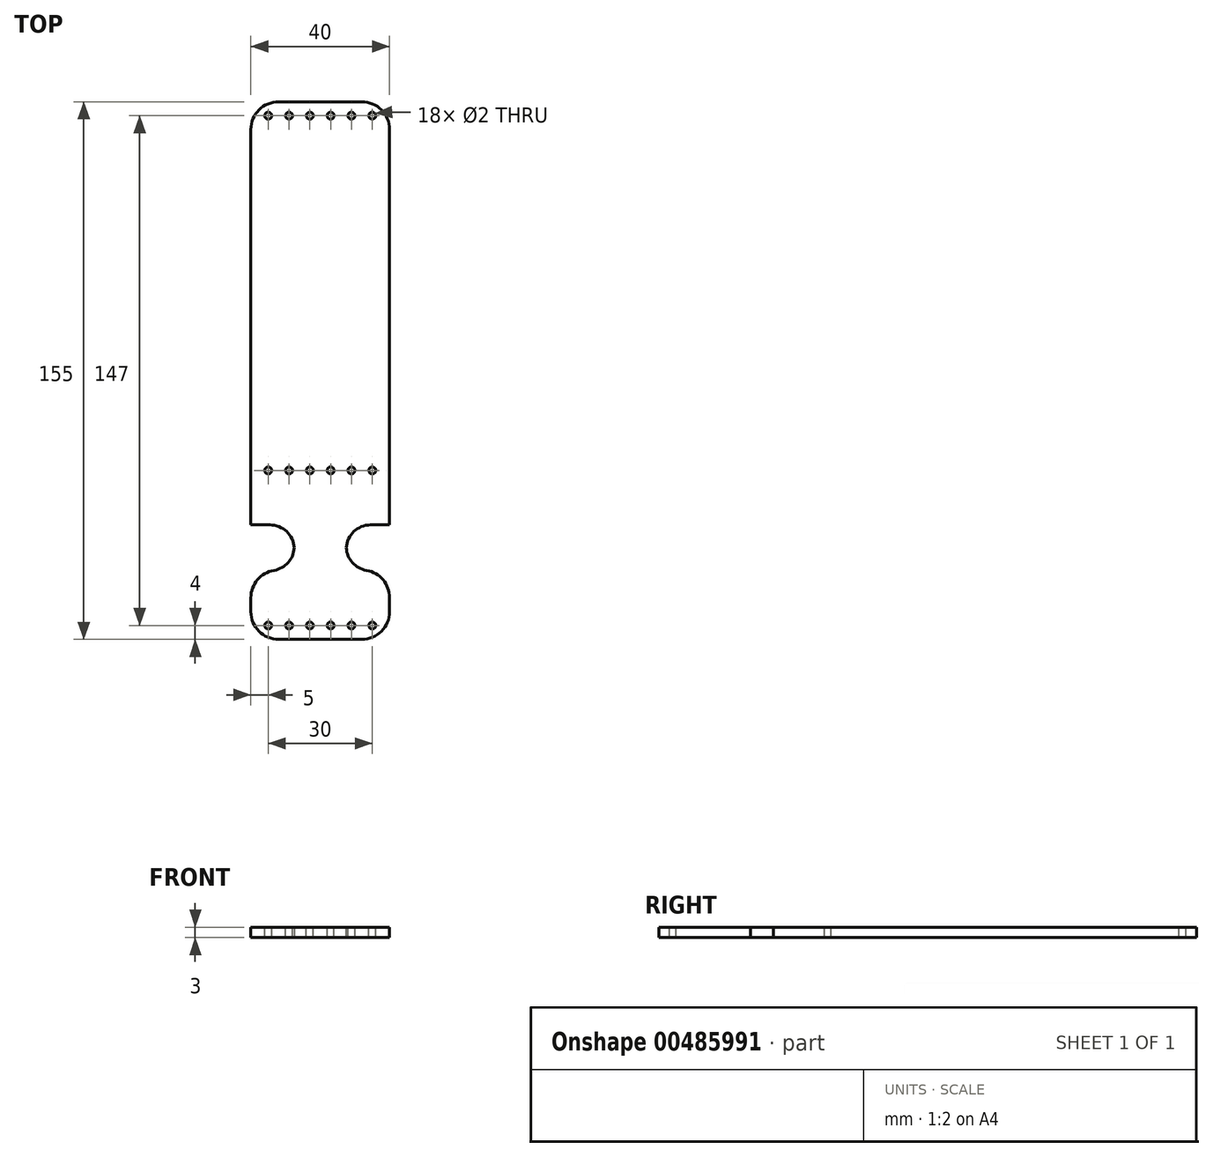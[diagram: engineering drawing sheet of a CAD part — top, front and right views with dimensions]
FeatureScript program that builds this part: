
annotation { "Feature Type Name" : "Feature", "Feature Type Description" : "" }
export const myFeature = defineFeature(function(context is Context, id is Id, definition is map)
    precondition{}
    {
        {
            var Q0;
            Q0=qCreatedBy(makeId("Top.planeOp"),FACE);
            var sketch = newSketch(context, id + "F0", { "sketchPlane" : qUnion([Q0])});
            skLineSegment(sketch, "E0.bottom", {"start": v(-20, 77.5) * mm, "end": v(20, 77.5) * mm});
            skLineSegment(sketch, "E0.top", {"start": v(-20, -77.5) * mm, "end": v(20, -77.5) * mm});
            skLineSegment(sketch, "E0.left", {"start": v(-20, 77.5) * mm, "end": v(-20, -77.5) * mm});
            skLineSegment(sketch, "E0.right", {"start": v(20, 77.5) * mm, "end": v(20, -77.5) * mm});
            skSolve(sketch);
        }
        {
            var Q0;
            Q0=qSketchRegion(id+"F0",true);
            extrude(context, id + "F1", {"entities" : qUnion([Q0]), "depth" : 3 * mm});
        }
        {
            var Q0;
            Q0=makeQuery(id+"F1.opExtrude","CAP_FACE",FACE,{"disambiguationData":[OSD([sQuery(id+"F0.wireOp",EDGE,"E0.bottom"),sQuery(id+"F0.wireOp",EDGE,"E0.top"),sQuery(id+"F0.wireOp",EDGE,"E0.left"),sQuery(id+"F0.wireOp",EDGE,"E0.right")])],"isStart":false});
            var sketch = newSketch(context, id + "F2", { "sketchPlane" : qUnion([Q0])});
            skLineSegment(sketch, "E1.bottom", {"start": v(-20, -57.5) * mm, "end": v(20, -57.5) * mm});
            skLineSegment(sketch, "E1.top", {"start": v(-20, -44.5) * mm, "end": v(20, -44.5) * mm});
            skLineSegment(sketch, "E1.left", {"start": v(-20, -57.5) * mm, "end": v(-20, -44.5) * mm});
            skLineSegment(sketch, "E1.right", {"start": v(20, -57.5) * mm, "end": v(20, -44.5) * mm});
            skLineSegment(sketch, "E2.bottom", {"start": v(-7.5, -44.5) * mm, "end": v(7.5, -44.5) * mm});
            skLineSegment(sketch, "E2.top", {"start": v(-7.5, -57.5) * mm, "end": v(7.5, -57.5) * mm});
            skLineSegment(sketch, "E2.left", {"start": v(-7.5, -44.5) * mm, "end": v(-7.5, -57.5) * mm});
            skLineSegment(sketch, "E2.right", {"start": v(7.5, -44.5) * mm, "end": v(7.5, -57.5) * mm});
            skSolve(sketch);
        }
        {
            var Q0;
            {var subQ0=sQuery(id+"F2.wireOp",EDGE,"E1.left");Q0=makeQuery(id+"F2.imprint","IMPRINT",FACE,{"disambiguationData":[TD([[makeQuery(id+"F2.imprint","IMPRINT",EDGE,{"derivedFrom":subQ0}),1.0]])]});}
            var Q1;
            {var subQ0=sQuery(id+"F2.wireOp",EDGE,"E1.right");Q1=makeQuery(id+"F2.imprint","IMPRINT",FACE,{"disambiguationData":[TD([[makeQuery(id+"F2.imprint","IMPRINT",EDGE,{"derivedFrom":subQ0}),-1.0]])]});}
            extrude(context, id + "F3", {"entities" : qUnion([Q0, Q1]), "operationType" : NewBodyOperationType.REMOVE, "endBound" : BoundingType.UP_TO_NEXT, "oppositeDirection" : true, "depth" : 25 * mm});
        }
        {
            var Q0;
            Q0=makeQuery(id+"F3.boolean.opBoolean","COPY",EDGE,{"derivedFrom":makeQuery(id+"F3.opExtrude","SWEPT_EDGE",EDGE,{"disambiguationData":[OSD([sQuery(id+"F0.wireOp",EDGE,"E0.left"),sQuery(id+"F2.wireOp",EDGE,"E1.top"),sQuery(id+"F2.wireOp",EDGE,"E1.left")])]})});
            var Q1;
            Q1=makeQuery(id+"F3.boolean.opBoolean","COPY",EDGE,{"derivedFrom":makeQuery(id+"F3.opExtrude","SWEPT_EDGE",EDGE,{"disambiguationData":[OSD([sQuery(id+"F0.wireOp",EDGE,"E0.right"),sQuery(id+"F2.wireOp",EDGE,"E1.top"),sQuery(id+"F2.wireOp",EDGE,"E1.right")])]})});
            var Q2;
            Q2=makeQuery(id+"F3.boolean.opBoolean","COPY",EDGE,{"derivedFrom":makeQuery(id+"F3.opExtrude","SWEPT_EDGE",EDGE,{"disambiguationData":[OSD([sQuery(id+"F0.wireOp",EDGE,"E0.right"),sQuery(id+"F2.wireOp",EDGE,"E1.bottom"),sQuery(id+"F2.wireOp",EDGE,"E1.right")])]})});
            var Q3;
            Q3=makeQuery(id+"F3.boolean.opBoolean","COPY",EDGE,{"derivedFrom":makeQuery(id+"F3.opExtrude","SWEPT_EDGE",EDGE,{"disambiguationData":[OSD([sQuery(id+"F0.wireOp",EDGE,"E0.left"),sQuery(id+"F2.wireOp",EDGE,"E1.bottom"),sQuery(id+"F2.wireOp",EDGE,"E1.left")])]})});
            var Q4;
            Q4=makeQuery(id+"F1.opExtrude","SWEPT_EDGE",EDGE,{"disambiguationData":[OSD([sQuery(id+"F0.wireOp",EDGE,"E0.top"),sQuery(id+"F0.wireOp",EDGE,"E0.left")])]});
            var Q5;
            Q5=makeQuery(id+"F1.opExtrude","SWEPT_EDGE",EDGE,{"disambiguationData":[OSD([sQuery(id+"F0.wireOp",EDGE,"E0.top"),sQuery(id+"F0.wireOp",EDGE,"E0.right")])]});
            var Q6;
            Q6=makeQuery(id+"F1.opExtrude","SWEPT_EDGE",EDGE,{"disambiguationData":[OSD([sQuery(id+"F0.wireOp",EDGE,"E0.bottom"),sQuery(id+"F0.wireOp",EDGE,"E0.left")])]});
            var Q7;
            Q7=makeQuery(id+"F1.opExtrude","SWEPT_EDGE",EDGE,{"disambiguationData":[OSD([sQuery(id+"F0.wireOp",EDGE,"E0.bottom"),sQuery(id+"F0.wireOp",EDGE,"E0.right")])]});
            fillet(context, id + "F4", {"entities" : qUnion([Q0, Q1, Q2, Q3, Q4, Q5, Q6, Q7]), "radius" : 8 * mm, "tangentPropagation" : true, "allowEdgeOverflow" : false});
        }
        {
            var Q0;
            Q0=makeQuery(id+"F3.boolean.opBoolean","COPY",EDGE,{"derivedFrom":makeQuery(id+"F3.opExtrude","SWEPT_EDGE",EDGE,{"disambiguationData":[OSD([sQuery(id+"F2.wireOp",EDGE,"E1.top"),sQuery(id+"F2.wireOp",EDGE,"E2.bottom"),sQuery(id+"F2.wireOp",EDGE,"E2.left")])]})});
            var Q1;
            Q1=makeQuery(id+"F3.boolean.opBoolean","COPY",EDGE,{"derivedFrom":makeQuery(id+"F3.opExtrude","SWEPT_EDGE",EDGE,{"disambiguationData":[OSD([sQuery(id+"F2.wireOp",EDGE,"E1.bottom"),sQuery(id+"F2.wireOp",EDGE,"E2.top"),sQuery(id+"F2.wireOp",EDGE,"E2.left")])]})});
            var Q2;
            Q2=makeQuery(id+"F3.boolean.opBoolean","COPY",EDGE,{"derivedFrom":makeQuery(id+"F3.opExtrude","SWEPT_EDGE",EDGE,{"disambiguationData":[OSD([sQuery(id+"F2.wireOp",EDGE,"E1.top"),sQuery(id+"F2.wireOp",EDGE,"E2.bottom"),sQuery(id+"F2.wireOp",EDGE,"E2.right")])]})});
            var Q3;
            Q3=makeQuery(id+"F3.boolean.opBoolean","COPY",EDGE,{"derivedFrom":makeQuery(id+"F3.opExtrude","SWEPT_EDGE",EDGE,{"disambiguationData":[OSD([sQuery(id+"F2.wireOp",EDGE,"E1.bottom"),sQuery(id+"F2.wireOp",EDGE,"E2.top"),sQuery(id+"F2.wireOp",EDGE,"E2.right")])]})});
            fillet(context, id + "F5", {"entities" : qUnion([Q0, Q1, Q2, Q3]), "radius" : 7 * mm, "tangentPropagation" : true, "allowEdgeOverflow" : false});
        }
        {
            var Q0;
            Q0=makeQuery(id+"F1.opExtrude","CAP_FACE",FACE,{"disambiguationData":[OSD([sQuery(id+"F0.wireOp",EDGE,"E0.bottom"),sQuery(id+"F0.wireOp",EDGE,"E0.top"),sQuery(id+"F0.wireOp",EDGE,"E0.left"),sQuery(id+"F0.wireOp",EDGE,"E0.right")])],"isStart":false});
            var sketch = newSketch(context, id + "F6", { "sketchPlane" : qUnion([Q0])});
            skCircle(sketch, "E3", {"center": v(-15, -73.5) * mm, "radius": 1 * mm});
            skCircle(sketch, "E4.1.0.0", {"center": v(-9, -73.5) * mm, "radius": 1 * mm});
            skCircle(sketch, "E4.2.0.0", {"center": v(-3, -73.5) * mm, "radius": 1 * mm});
            skCircle(sketch, "E4.3.0.0", {"center": v(3, -73.5) * mm, "radius": 1 * mm});
            skLineSegment(sketch, "E4.direction1", {"start": v(-15, -73.5) * mm, "end": v(-9, -73.5) * mm, "construction": true});
            skCircle(sketch, "E5", {"center": v(-15, -28.8) * mm, "radius": 1 * mm});
            skCircle(sketch, "E6.1.0.0", {"center": v(-9, -28.8) * mm, "radius": 1 * mm});
            skCircle(sketch, "E6.2.0.0", {"center": v(-3, -28.8) * mm, "radius": 1 * mm});
            skCircle(sketch, "E6.3.0.0", {"center": v(3, -28.8) * mm, "radius": 1 * mm});
            skLineSegment(sketch, "E6.direction1", {"start": v(-15, -28.8) * mm, "end": v(-9, -28.8) * mm, "construction": true});
            skCircle(sketch, "E7", {"center": v(-15, 73.5) * mm, "radius": 1 * mm});
            skCircle(sketch, "E8.1.0.0", {"center": v(-9, 73.5) * mm, "radius": 1 * mm});
            skCircle(sketch, "E8.2.0.0", {"center": v(-3, 73.5) * mm, "radius": 1 * mm});
            skCircle(sketch, "E8.3.0.0", {"center": v(3, 73.5) * mm, "radius": 1 * mm});
            skLineSegment(sketch, "E8.direction1", {"start": v(-15, 73.5) * mm, "end": v(-9, 73.5) * mm, "construction": true});
            skCircle(sketch, "E9.0.4.0", {"center": v(9, -73.5) * mm, "radius": 1 * mm});
            skCircle(sketch, "E9.0.5.0", {"center": v(15, -73.5) * mm, "radius": 1 * mm});
            skCircle(sketch, "E10.0.4.0", {"center": v(9, -28.8) * mm, "radius": 1 * mm});
            skCircle(sketch, "E10.0.5.0", {"center": v(15, -28.8) * mm, "radius": 1 * mm});
            skCircle(sketch, "E11.0.4.0", {"center": v(9, 73.5) * mm, "radius": 1 * mm});
            skCircle(sketch, "E11.0.5.0", {"center": v(15, 73.5) * mm, "radius": 1 * mm});
            skSolve(sketch);
        }
        {
            var Q0;
            Q0=qSketchRegion(id+"F6",true);
            extrude(context, id + "F7", {"entities" : qUnion([Q0]), "operationType" : NewBodyOperationType.REMOVE, "endBound" : BoundingType.UP_TO_NEXT, "oppositeDirection" : true, "depth" : 25 * mm});
        }
    });
